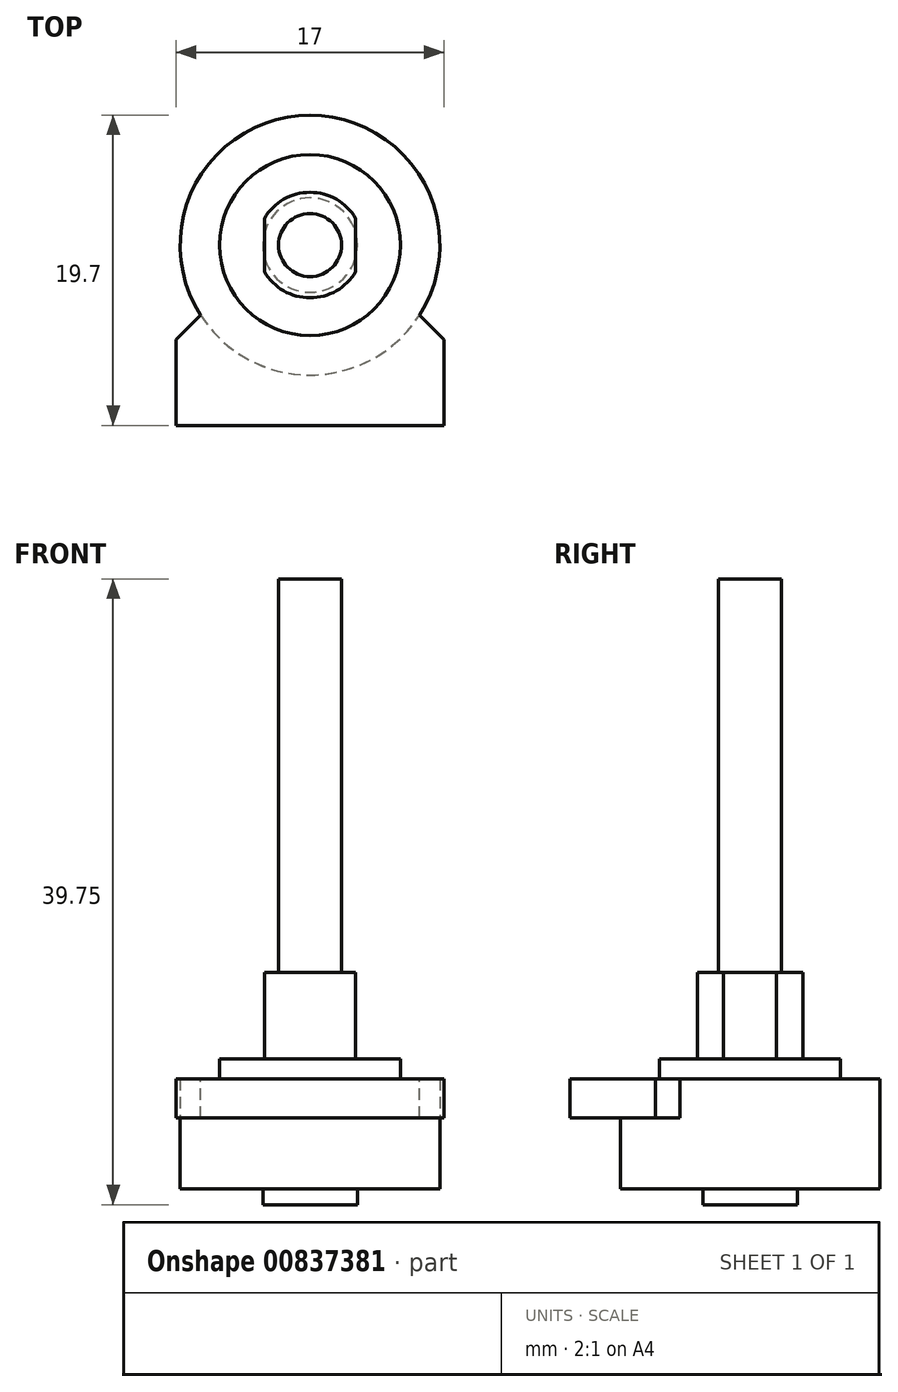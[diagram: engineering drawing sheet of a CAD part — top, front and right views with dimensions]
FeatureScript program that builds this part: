
annotation { "Feature Type Name" : "Feature", "Feature Type Description" : "" }
export const myFeature = defineFeature(function(context is Context, id is Id, definition is map)
    precondition{}
    {
        {
            var Q0;
            Q0=qCreatedBy(makeId("Top.planeOp"),FACE);
            var sketch = newSketch(context, id + "F0", { "sketchPlane" : qUnion([Q0])});
            skCircle(sketch, "E0", {"center": v(0, 0) * mm, "radius": 8.25 * mm});
            skSolve(sketch);
        }
        {
            var Q0;
            Q0=makeQuery(id+"F0.imprint","IMPRINT",FACE,{"disambiguationData":[TD([[makeQuery(id+"F0.imprint","IMPRINT",EDGE,{"derivedFrom":sQuery(id+"F0.wireOp",EDGE,"E0")}),1.0]])]});
            extrude(context, id + "F1", {"entities" : qUnion([Q0]), "depth" : 7 * mm, "offsetDistance" : 25 * mm});
        }
        {
            var Q0;
            Q0=makeQuery(id+"F1.opExtrude","CAP_FACE",FACE,{"disambiguationData":[OSD([sQuery(id+"F0.wireOp",EDGE,"E0")])],"isStart":true});
            var sketch = newSketch(context, id + "F2", { "sketchPlane" : qUnion([Q0])});
            skCircle(sketch, "E1", {"center": v(0, 0) * mm, "radius": 3 * mm});
            skSolve(sketch);
        }
        {
            var Q0;
            Q0=makeQuery(id+"F2.imprint","IMPRINT",FACE,{"disambiguationData":[TD([[makeQuery(id+"F2.imprint","IMPRINT",EDGE,{"derivedFrom":sQuery(id+"F2.wireOp",EDGE,"E1")}),1.0]])]});
            extrude(context, id + "F3", {"entities" : qUnion([Q0]), "operationType" : NewBodyOperationType.ADD, "depth" : 1 * mm, "offsetDistance" : 25 * mm});
        }
        {
            var Q0;
            Q0=makeQuery(id+"F1.opExtrude","CAP_FACE",FACE,{"disambiguationData":[OSD([sQuery(id+"F0.wireOp",EDGE,"E0")])],"isStart":false});
            var sketch = newSketch(context, id + "F4", { "sketchPlane" : qUnion([Q0])});
            skCircle(sketch, "E2", {"center": v(0, 0) * mm, "radius": 5.75 * mm});
            skSolve(sketch);
        }
        {
            var Q0;
            Q0 = qSketchRegion(id + "F4", true);
            extrude(context, id + "F5", {"entities" : qUnion([Q0]), "operationType" : NewBodyOperationType.ADD, "depth" : 1.25 * mm, "offsetDistance" : 25 * mm});
        }
        {
            var Q0;
            Q0=makeQuery(id+"F5.opExtrude","CAP_FACE",FACE,{"disambiguationData":[OSD([sQuery(id+"F4.wireOp",EDGE,"E2")])],"isStart":false});
            var sketch = newSketch(context, id + "F6", { "sketchPlane" : qUnion([Q0])});
            skCircle(sketch, "E3", {"center": v(0, 0) * mm, "radius": 3.35 * mm});
            skSolve(sketch);
        }
        {
            var Q0;
            Q0 = qSketchRegion(id + "F6", true);
            extrude(context, id + "F7", {"entities" : qUnion([Q0]), "operationType" : NewBodyOperationType.ADD, "depth" : 5.5 * mm, "offsetDistance" : 25 * mm});
        }
        {
            var Q0;
            Q0=makeQuery(id+"F7.opExtrude","CAP_FACE",FACE,{"disambiguationData":[OSD([sQuery(id+"F6.wireOp",EDGE,"E3")])],"isStart":false});
            var sketch = newSketch(context, id + "F8", { "sketchPlane" : qUnion([Q0])});
            skLineSegment(sketch, "E4.bottom", {"start": v(2.9, -3.35) * mm, "end": v(-2.9, -3.35) * mm});
            skLineSegment(sketch, "E4.top", {"start": v(2.9, 3.35) * mm, "end": v(-2.9, 3.35) * mm});
            skLineSegment(sketch, "E4.left", {"start": v(2.9, -3.35) * mm, "end": v(2.9, 3.35) * mm});
            skLineSegment(sketch, "E4.right", {"start": v(-2.9, -3.35) * mm, "end": v(-2.9, 3.35) * mm});
            skPoint(sketch, "E4.middle", {"position": v(0, 0) * mm});
            skArc(sketch, "E5", {"start": v(-2.9, 1.68) * mm, "mid": v(-3.35, 0) * mm, "end": v(-2.9, -1.68) * mm});
            skArc(sketch, "E6", {"start": v(2.9, -1.68) * mm, "mid": v(3.35, 0) * mm, "end": v(2.9, 1.68) * mm});
            skSolve(sketch);
        }
        {
            var Q0;
            {var subQ0=sQuery(id+"F8.wireOp",EDGE,"E5");Q0=makeQuery(id+"F8.imprint","IMPRINT",FACE,{"disambiguationData":[TD([[makeQuery(id+"F8.imprint","IMPRINT",EDGE,{"derivedFrom":subQ0}),1.0]])]});}
            var Q1;
            {var subQ0=sQuery(id+"F8.wireOp",EDGE,"E6");Q1=makeQuery(id+"F8.imprint","IMPRINT",FACE,{"disambiguationData":[TD([[makeQuery(id+"F8.imprint","IMPRINT",EDGE,{"derivedFrom":subQ0}),1.0]])]});}
            var Q2;
            Q2=makeQuery(id+"F5.opExtrude","CAP_FACE",FACE,{"disambiguationData":[OSD([sQuery(id+"F4.wireOp",EDGE,"E2")])],"isStart":false});
            extrude(context, id + "F9", {"entities" : qUnion([Q0, Q1]), "operationType" : NewBodyOperationType.REMOVE, "endBound" : BoundingType.UP_TO_SURFACE, "oppositeDirection" : true, "depth" : 25 * mm, "endBoundEntityFace" : qUnion([Q2]), "offsetDistance" : 25 * mm});
        }
        {
            var Q0;
            Q0=makeQuery(id+"F7.opExtrude","CAP_FACE",FACE,{"disambiguationData":[OSD([sQuery(id+"F6.wireOp",EDGE,"E3")])],"isStart":false});
            var sketch = newSketch(context, id + "F10", { "sketchPlane" : qUnion([Q0])});
            skCircle(sketch, "E7", {"center": v(0, 0) * mm, "radius": 2 * mm});
            skSolve(sketch);
        }
        {
            var Q0;
            Q0=makeQuery(id+"F10.imprint","IMPRINT",FACE,{"disambiguationData":[TD([[makeQuery(id+"F10.imprint","IMPRINT",EDGE,{"derivedFrom":sQuery(id+"F10.wireOp",EDGE,"E7")}),1.0]])]});
            extrude(context, id + "F11", {"entities" : qUnion([Q0]), "operationType" : NewBodyOperationType.ADD, "depth" : 25 * mm, "offsetDistance" : 25 * mm});
        }
        {
            var Q0;
            Q0=makeQuery(id+"F1.opExtrude","CAP_FACE",FACE,{"disambiguationData":[OSD([sQuery(id+"F0.wireOp",EDGE,"E0")])],"isStart":false});
            var sketch = newSketch(context, id + "F12", { "sketchPlane" : qUnion([Q0])});
            skLineSegment(sketch, "E8.bottom", {"start": v(8.5, -11.45) * mm, "end": v(-8.5, -11.45) * mm});
            skLineSegment(sketch, "E8.top", {"start": v(8.5, -4.45) * mm, "end": v(-8.5, -4.45) * mm});
            skLineSegment(sketch, "E8.left", {"start": v(8.5, -11.45) * mm, "end": v(8.5, -4.45) * mm});
            skLineSegment(sketch, "E8.right", {"start": v(-8.5, -11.45) * mm, "end": v(-8.5, -4.45) * mm});
            skPoint(sketch, "E8.middle", {"position": v(0, -7.95) * mm});
            skLineSegment(sketch, "E9", {"start": v(-7.92, 8.25) * mm, "end": v(12.17, 8.25) * mm, "construction": true});
            skLineSegment(sketch, "E10", {"start": v(-6.95, -4.45) * mm, "end": v(-8.5, -6) * mm});
            skLineSegment(sketch, "E11", {"start": v(6.95, -4.45) * mm, "end": v(8.5, -6) * mm});
            skSolve(sketch);
        }
        {
            var Q0;
            {var subQ1=sQuery(id+"F12.wireOp",EDGE,"E8.bottom");Q0=makeQuery(id+"F12.imprint","IMPRINT",FACE,{"disambiguationData":[TD([[makeQuery(id+"F12.imprint","IMPRINT",EDGE,{"derivedFrom":subQ1}),-1.0]])]});}
            extrude(context, id + "F13", {"entities" : qUnion([Q0]), "operationType" : NewBodyOperationType.ADD, "oppositeDirection" : true, "depth" : 2.5 * mm, "offsetDistance" : 25 * mm});
        }
    });
